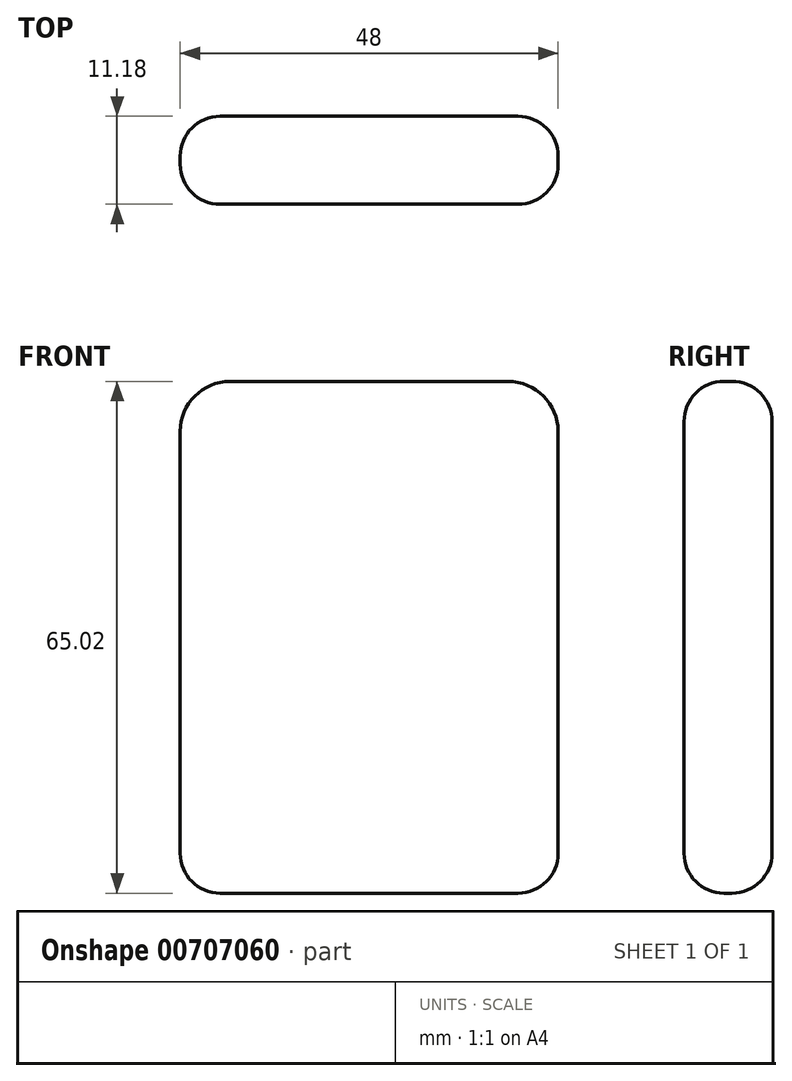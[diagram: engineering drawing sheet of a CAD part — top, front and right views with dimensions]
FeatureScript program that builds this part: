
annotation { "Feature Type Name" : "Feature", "Feature Type Description" : "" }
export const myFeature = defineFeature(function(context is Context, id is Id, definition is map)
    precondition{}
    {
        {
            var Q0;
            Q0=qCreatedBy(makeId("Front.planeOp"),FACE);
            var sketch = newSketch(context, id + "F0", { "sketchPlane" : qUnion([Q0])});
            skLineSegment(sketch, "E0.bottom", {"start": v(24, -32.51) * mm, "end": v(-24, -32.51) * mm});
            skLineSegment(sketch, "E0.top", {"start": v(17.65, 32.51) * mm, "end": v(-17.65, 32.51) * mm});
            skLineSegment(sketch, "E0.left", {"start": v(24, -32.51) * mm, "end": v(24, 26.16) * mm});
            skLineSegment(sketch, "E0.right", {"start": v(-24, -32.51) * mm, "end": v(-24, 26.16) * mm});
            skPoint(sketch, "E0.middle", {"position": v(0, 0) * mm});
            skPoint(sketch, "E1.visualSharp", {"position": v(-24, 32.51) * mm});
            skArc(sketch, "E1.filletArc", {"start": v(-17.65, 32.51) * mm, "mid": v(-22.14, 30.65) * mm, "end": v(-24, 26.16) * mm});
            skPoint(sketch, "E2.visualSharp", {"position": v(24, 32.51) * mm});
            skArc(sketch, "E2.filletArc", {"start": v(24, 26.16) * mm, "mid": v(22.14, 30.65) * mm, "end": v(17.65, 32.51) * mm});
            skSolve(sketch);
        }
        {
            var Q0;
            Q0=makeQuery(id+"F0.imprint","IMPRINT",FACE,{"disambiguationData":[TD([[makeQuery(id+"F0.imprint","IMPRINT",EDGE,{"derivedFrom":sQuery(id+"F0.wireOp",EDGE,"E0.bottom")}),-1.0]])]});
            extrude(context, id + "F1", {"entities" : qUnion([Q0]), "endBound" : BoundingType.SYMMETRIC, "depth" : 11.18 * mm, "offsetDistance" : 25.4 * mm});
        }
        {
            var Q0;
            Q0=makeQuery(id+"F1.opExtrude","SWEPT_FACE",FACE,{"disambiguationData":[OSD([sQuery(id+"F0.wireOp",EDGE,"E1.filletArc")])]});
            fillet(context, id + "F2", {"entities" : qUnion([Q0]), "radius" : 5.08 * mm, "tangentPropagation" : true, "allowEdgeOverflow" : false});
        }
        {
            var Q0;
            Q0=makeQuery(id+"F2.opFillet","BLEND_EDGE",EDGE,{"blendedFrom":[makeQuery(id+"F1.opExtrude","CAP_EDGE",EDGE,{"disambiguationData":[OSD([sQuery(id+"F0.wireOp",EDGE,"E0.right")])],"isStart":false}),makeQuery(id+"F1.opExtrude","SWEPT_FACE",FACE,{"disambiguationData":[OSD([sQuery(id+"F0.wireOp",EDGE,"E0.bottom")])]})],"blendedInto":[makeQuery(id+"F1.opExtrude","SWEPT_FACE",FACE,{"disambiguationData":[OSD([sQuery(id+"F0.wireOp",EDGE,"E0.bottom")])]})]});
            var Q1;
            Q1=makeQuery(id+"F2.opFillet","BLEND_EDGE",EDGE,{"blendedFrom":[makeQuery(id+"F1.opExtrude","CAP_EDGE",EDGE,{"disambiguationData":[OSD([sQuery(id+"F0.wireOp",EDGE,"E0.left")])],"isStart":false}),makeQuery(id+"F1.opExtrude","SWEPT_FACE",FACE,{"disambiguationData":[OSD([sQuery(id+"F0.wireOp",EDGE,"E0.bottom")])]})],"blendedInto":[makeQuery(id+"F1.opExtrude","SWEPT_FACE",FACE,{"disambiguationData":[OSD([sQuery(id+"F0.wireOp",EDGE,"E0.bottom")])]})]});
            fillet(context, id + "F3", {"entities" : qUnion([Q0, Q1]), "radius" : 5.08 * mm, "tangentPropagation" : true, "allowEdgeOverflow" : false});
        }
    });
